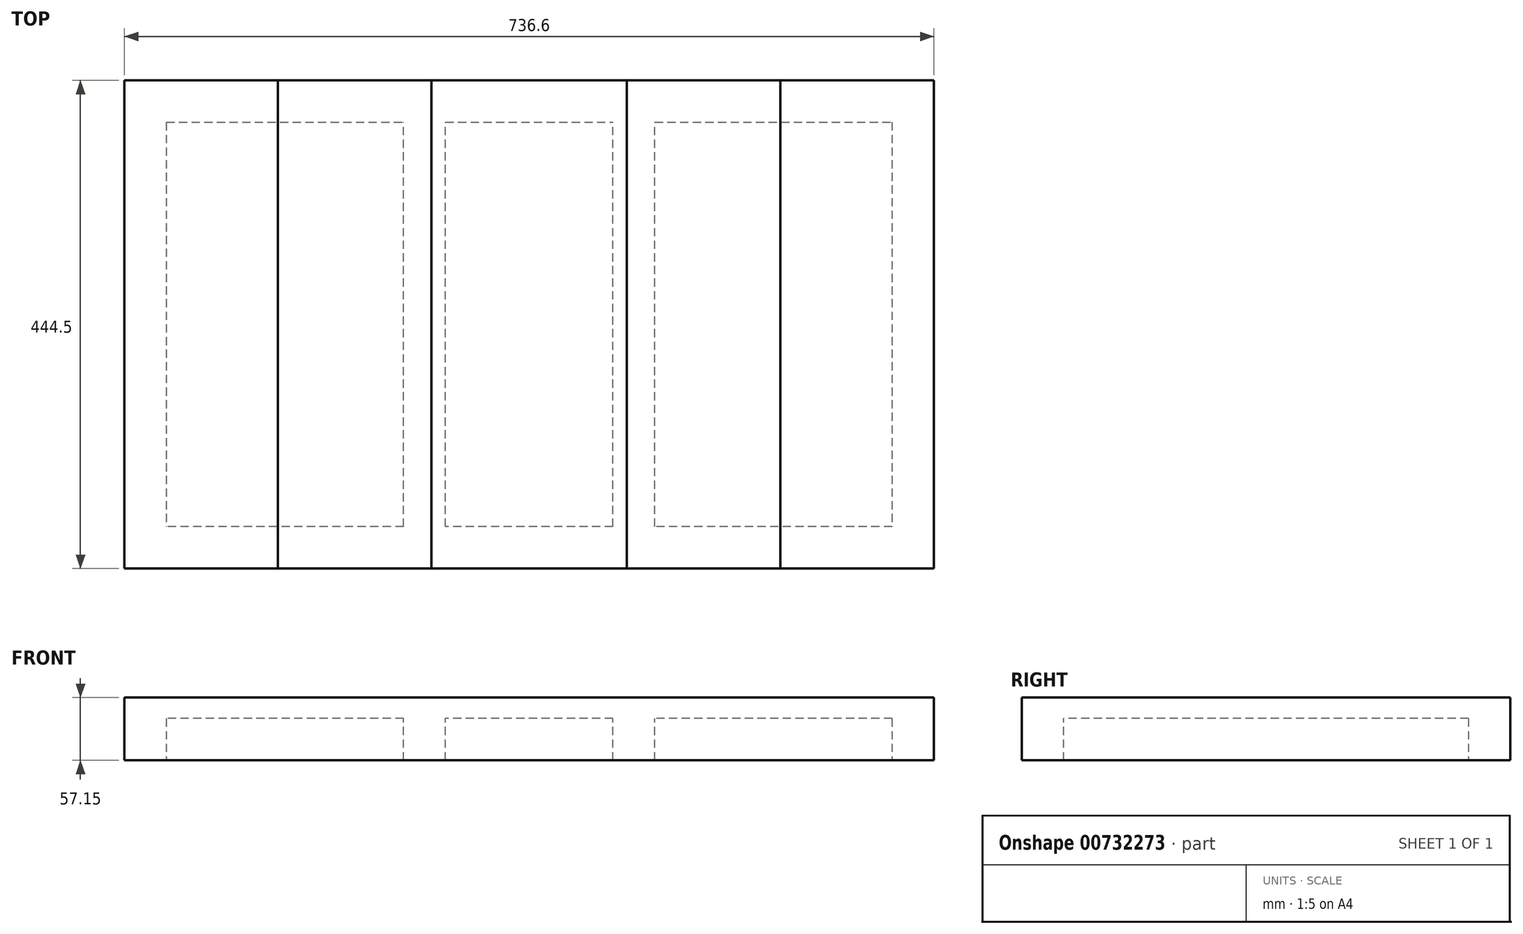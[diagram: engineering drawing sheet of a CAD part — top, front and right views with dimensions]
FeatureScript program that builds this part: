
annotation { "Feature Type Name" : "Feature", "Feature Type Description" : "" }
export const myFeature = defineFeature(function(context is Context, id is Id, definition is map)
    precondition{}
    {
        {
            var Q0;
            Q0=qCreatedBy(makeId("Right.planeOp"),FACE);
            var sketch = newSketch(context, id + "F0", { "sketchPlane" : qUnion([Q0])});
            skLineSegment(sketch, "E0.bottom", {"start": v(0, 0) * mm, "end": v(-38.1, 0) * mm});
            skLineSegment(sketch, "E0.top", {"start": v(0, -38.1) * mm, "end": v(-38.1, -38.1) * mm});
            skLineSegment(sketch, "E0.left", {"start": v(0, 0) * mm, "end": v(0, -38.1) * mm});
            skLineSegment(sketch, "E0.right", {"start": v(-38.1, 0) * mm, "end": v(-38.1, -38.1) * mm});
            skSolve(sketch);
        }
        {
            var Q0;
            Q0=makeQuery(id+"F0.imprint","IMPRINT",FACE,{"disambiguationData":[TD([[makeQuery(id+"F0.imprint","IMPRINT",EDGE,{"derivedFrom":sQuery(id+"F0.wireOp",EDGE,"E0.bottom")}),1.0]])]});
            extrude(context, id + "F1", {"entities" : qUnion([Q0]), "depth" : 736.6 * mm, "offsetDistance" : 25.4 * mm});
        }
        {
            var Q0;
            Q0=makeQuery(id+"F1.opExtrude","SWEPT_FACE",FACE,{"disambiguationData":[OSD([sQuery(id+"F0.wireOp",EDGE,"E0.left")])]});
            var sketch = newSketch(context, id + "F2", { "sketchPlane" : qUnion([Q0])});
            skLineSegment(sketch, "E1.bottom", {"start": v(-736.6, 0) * mm, "end": v(-698.5, 0) * mm});
            skLineSegment(sketch, "E1.top", {"start": v(-736.6, -38.1) * mm, "end": v(-698.5, -38.1) * mm});
            skLineSegment(sketch, "E1.left", {"start": v(-736.6, 0) * mm, "end": v(-736.6, -38.1) * mm});
            skLineSegment(sketch, "E1.right", {"start": v(-698.5, 0) * mm, "end": v(-698.5, -38.1) * mm});
            skLineSegment(sketch, "E2.bottom", {"start": v(0, 0) * mm, "end": v(-38.1, 0) * mm});
            skLineSegment(sketch, "E2.top", {"start": v(0, -38.1) * mm, "end": v(-38.1, -38.1) * mm});
            skLineSegment(sketch, "E2.left", {"start": v(0, 0) * mm, "end": v(0, -38.1) * mm});
            skLineSegment(sketch, "E2.right", {"start": v(-38.1, 0) * mm, "end": v(-38.1, -38.1) * mm});
            skSolve(sketch);
        }
        {
            var Q0;
            Q0=makeQuery(id+"F2.imprint","IMPRINT",FACE,{"disambiguationData":[TD([[makeQuery(id+"F2.imprint","IMPRINT",EDGE,{"derivedFrom":sQuery(id+"F2.wireOp",EDGE,"E2.bottom")}),-1.0]])]});
            var Q1;
            Q1=makeQuery(id+"F2.imprint","IMPRINT",FACE,{"disambiguationData":[TD([[makeQuery(id+"F2.imprint","IMPRINT",EDGE,{"derivedFrom":sQuery(id+"F2.wireOp",EDGE,"E1.bottom")}),-1.0]])]});
            extrude(context, id + "F3", {"entities" : qUnion([Q0, Q1]), "operationType" : NewBodyOperationType.ADD, "depth" : 368.3 * mm, "offsetDistance" : 25.4 * mm});
        }
        {
            var Q0;
            Q0=makeQuery(id+"F3.boolean.opBoolean","MERGE",FACE,{"derivedFrom":[makeQuery(id+"F1.opExtrude","CAP_FACE",FACE,{"disambiguationData":[OSD([sQuery(id+"F0.wireOp",EDGE,"E0.bottom"),sQuery(id+"F0.wireOp",EDGE,"E0.top"),sQuery(id+"F0.wireOp",EDGE,"E0.left"),sQuery(id+"F0.wireOp",EDGE,"E0.right")])],"isStart":false}),makeQuery(id+"F3.opExtrude","SWEPT_FACE",FACE,{"disambiguationData":[OSD([sQuery(id+"F2.wireOp",EDGE,"E1.left")])]})]});
            var sketch = newSketch(context, id + "F4", { "sketchPlane" : qUnion([Q0])});
            skLineSegment(sketch, "E3.bottom", {"start": v(368.3, 0) * mm, "end": v(406.4, 0) * mm});
            skLineSegment(sketch, "E3.top", {"start": v(368.3, -38.1) * mm, "end": v(406.4, -38.1) * mm});
            skLineSegment(sketch, "E3.left", {"start": v(368.3, 0) * mm, "end": v(368.3, -38.1) * mm});
            skLineSegment(sketch, "E3.right", {"start": v(406.4, 0) * mm, "end": v(406.4, -38.1) * mm});
            skSolve(sketch);
        }
        {
            var Q0;
            Q0=makeQuery(id+"F4.imprint","IMPRINT",FACE,{"disambiguationData":[TD([[makeQuery(id+"F4.imprint","IMPRINT",EDGE,{"derivedFrom":sQuery(id+"F4.wireOp",EDGE,"E3.bottom")}),-1.0]])]});
            extrude(context, id + "F5", {"entities" : qUnion([Q0]), "operationType" : NewBodyOperationType.ADD, "oppositeDirection" : true, "depth" : 736.6 * mm, "offsetDistance" : 25.4 * mm});
        }
        {
            var Q0;
            Q0=makeQuery(id+"F5.opExtrude","SWEPT_FACE",FACE,{"disambiguationData":[OSD([sQuery(id+"F4.wireOp",EDGE,"E3.left")])]});
            var sketch = newSketch(context, id + "F6", { "sketchPlane" : qUnion([Q0])});
            skLineSegment(sketch, "E4.bottom", {"start": v(254, 0) * mm, "end": v(292.1, 0) * mm});
            skLineSegment(sketch, "E4.top", {"start": v(254, -38.1) * mm, "end": v(292.1, -38.1) * mm});
            skLineSegment(sketch, "E4.left", {"start": v(254, 0) * mm, "end": v(254, -38.1) * mm});
            skLineSegment(sketch, "E4.right", {"start": v(292.1, 0) * mm, "end": v(292.1, -38.1) * mm});
            skLineSegment(sketch, "E5.bottom", {"start": v(444.5, 0) * mm, "end": v(482.6, 0) * mm});
            skLineSegment(sketch, "E5.top", {"start": v(444.5, -38.1) * mm, "end": v(482.6, -38.1) * mm});
            skLineSegment(sketch, "E5.left", {"start": v(444.5, 0) * mm, "end": v(444.5, -38.1) * mm});
            skLineSegment(sketch, "E5.right", {"start": v(482.6, 0) * mm, "end": v(482.6, -38.1) * mm});
            skSolve(sketch);
        }
        {
            var Q0;
            Q0=makeQuery(id+"F6.imprint","IMPRINT",FACE,{"disambiguationData":[TD([[makeQuery(id+"F6.imprint","IMPRINT",EDGE,{"derivedFrom":sQuery(id+"F6.wireOp",EDGE,"E4.bottom")}),-1.0]])]});
            var Q1;
            Q1=makeQuery(id+"F6.imprint","IMPRINT",FACE,{"disambiguationData":[TD([[makeQuery(id+"F6.imprint","IMPRINT",EDGE,{"derivedFrom":sQuery(id+"F6.wireOp",EDGE,"E5.bottom")}),-1.0]])]});
            extrude(context, id + "F7", {"entities" : qUnion([Q0, Q1]), "operationType" : NewBodyOperationType.ADD, "endBound" : BoundingType.UP_TO_NEXT, "depth" : 25.4 * mm, "offsetDistance" : 25.4 * mm});
        }
        {
            var Q0;
            Q0=makeQuery(id+"F7.boolean.opBoolean","MERGE",FACE,{"derivedFrom":[makeQuery(id+"F5.boolean.opBoolean","MERGE",FACE,{"derivedFrom":[makeQuery(id+"F3.boolean.opBoolean","MERGE",FACE,{"derivedFrom":[makeQuery(id+"F1.opExtrude","SWEPT_FACE",FACE,{"disambiguationData":[OSD([sQuery(id+"F0.wireOp",EDGE,"E0.bottom")])]}),makeQuery(id+"F3.opExtrude","SWEPT_FACE",FACE,{"disambiguationData":[OSD([sQuery(id+"F2.wireOp",EDGE,"E1.bottom")])]}),makeQuery(id+"F3.opExtrude","SWEPT_FACE",FACE,{"disambiguationData":[OSD([sQuery(id+"F2.wireOp",EDGE,"E2.bottom")])]})]}),makeQuery(id+"F5.opExtrude","SWEPT_FACE",FACE,{"disambiguationData":[OSD([sQuery(id+"F4.wireOp",EDGE,"E3.bottom")])]})]}),makeQuery(id+"F7.opExtrude","SWEPT_FACE",FACE,{"disambiguationData":[OSD([sQuery(id+"F6.wireOp",EDGE,"E4.bottom")])]}),makeQuery(id+"F7.opExtrude","SWEPT_FACE",FACE,{"disambiguationData":[OSD([sQuery(id+"F6.wireOp",EDGE,"E5.bottom")])]})]});
            var sketch = newSketch(context, id + "F8", { "sketchPlane" : qUnion([Q0])});
            skLineSegment(sketch, "E6.bottom", {"start": v(0, 406.4) * mm, "end": v(139.7, 406.4) * mm});
            skLineSegment(sketch, "E6.top", {"start": v(0, -38.1) * mm, "end": v(139.7, -38.1) * mm});
            skLineSegment(sketch, "E6.left", {"start": v(0, 406.4) * mm, "end": v(0, -38.1) * mm});
            skLineSegment(sketch, "E6.right", {"start": v(139.7, 406.4) * mm, "end": v(139.7, -38.1) * mm});
            skSolve(sketch);
        }
        {
            var Q0;
            {var subQ1=sQuery(id+"F8.wireOp",EDGE,"E6.bottom");Q0=makeQuery(id+"F8.imprint","IMPRINT",FACE,{"disambiguationData":[TD([[makeQuery(id+"F8.imprint","IMPRINT",EDGE,{"derivedFrom":subQ1}),-1.0]])]});}
            var Q1;
            {var subQ1=sQuery(id+"F2.wireOp",EDGE,"E2.right");var subQ5=sQuery(id+"F2.wireOp",EDGE,"E2.bottom");var subQ7=sQuery(id+"F0.wireOp",EDGE,"E0.bottom");var subQ17=sQuery(id+"F0.wireOp",EDGE,"E0.left");var subQ20=makeQuery(id+"F3.opExtrude","SWEPT_EDGE",EDGE,{"disambiguationData":[OSD([subQ7,subQ17,subQ5,subQ1])]});Q1=makeQuery(id+"F8.imprint","IMPRINT",FACE,{"disambiguationData":[TD([[makeQuery(id+"F8.imprint","IMPRINT",EDGE,{"derivedFrom":subQ20}),1.0]])]});}
            extrude(context, id + "F9", {"entities" : qUnion([Q0, Q1]), "operationType" : NewBodyOperationType.ADD, "depth" : 19.05 * mm, "offsetDistance" : 25.4 * mm});
        }
        {
            var Q0;
            Q0=makeQuery(id+"F7.boolean.opBoolean","MERGE",FACE,{"derivedFrom":[makeQuery(id+"F5.boolean.opBoolean","MERGE",FACE,{"derivedFrom":[makeQuery(id+"F3.boolean.opBoolean","MERGE",FACE,{"derivedFrom":[makeQuery(id+"F1.opExtrude","SWEPT_FACE",FACE,{"disambiguationData":[OSD([sQuery(id+"F0.wireOp",EDGE,"E0.bottom")])]}),makeQuery(id+"F3.opExtrude","SWEPT_FACE",FACE,{"disambiguationData":[OSD([sQuery(id+"F2.wireOp",EDGE,"E1.bottom")])]}),makeQuery(id+"F3.opExtrude","SWEPT_FACE",FACE,{"disambiguationData":[OSD([sQuery(id+"F2.wireOp",EDGE,"E2.bottom")])]})]}),makeQuery(id+"F5.opExtrude","SWEPT_FACE",FACE,{"disambiguationData":[OSD([sQuery(id+"F4.wireOp",EDGE,"E3.bottom")])]})]}),makeQuery(id+"F7.opExtrude","SWEPT_FACE",FACE,{"disambiguationData":[OSD([sQuery(id+"F6.wireOp",EDGE,"E4.bottom")])]}),makeQuery(id+"F7.opExtrude","SWEPT_FACE",FACE,{"disambiguationData":[OSD([sQuery(id+"F6.wireOp",EDGE,"E5.bottom")])]})]});
            var sketch = newSketch(context, id + "F10", { "sketchPlane" : qUnion([Q0])});
            skLineSegment(sketch, "E7.bottom", {"start": v(736.6, 406.4) * mm, "end": v(596.9, 406.4) * mm});
            skLineSegment(sketch, "E7.top", {"start": v(736.6, -38.1) * mm, "end": v(596.9, -38.1) * mm});
            skLineSegment(sketch, "E7.left", {"start": v(736.6, 406.4) * mm, "end": v(736.6, -38.1) * mm});
            skLineSegment(sketch, "E7.right", {"start": v(596.9, 406.4) * mm, "end": v(596.9, -38.1) * mm});
            skSolve(sketch);
        }
        {
            var Q0;
            {var subQ2=sQuery(id+"F2.wireOp",EDGE,"E1.right");var subQ6=sQuery(id+"F2.wireOp",EDGE,"E1.bottom");var subQ8=sQuery(id+"F0.wireOp",EDGE,"E0.bottom");var subQ16=sQuery(id+"F0.wireOp",EDGE,"E0.left");var subQ19=makeQuery(id+"F3.opExtrude","SWEPT_EDGE",EDGE,{"disambiguationData":[OSD([subQ8,subQ16,subQ6,subQ2])]});Q0=makeQuery(id+"F10.imprint","IMPRINT",FACE,{"disambiguationData":[TD([[makeQuery(id+"F10.imprint","IMPRINT",EDGE,{"derivedFrom":subQ19}),-1.0]])]});}
            var Q1;
            {var subQ1=sQuery(id+"F10.wireOp",EDGE,"E7.bottom");Q1=makeQuery(id+"F10.imprint","IMPRINT",FACE,{"disambiguationData":[TD([[makeQuery(id+"F10.imprint","IMPRINT",EDGE,{"derivedFrom":subQ1}),-1.0]])]});}
            extrude(context, id + "F11", {"entities" : qUnion([Q0, Q1]), "operationType" : NewBodyOperationType.ADD, "depth" : 19.05 * mm, "offsetDistance" : 25.4 * mm});
        }
        {
            var Q0;
            Q0=makeQuery(id+"F7.boolean.opBoolean","MERGE",FACE,{"derivedFrom":[makeQuery(id+"F5.boolean.opBoolean","MERGE",FACE,{"derivedFrom":[makeQuery(id+"F3.boolean.opBoolean","MERGE",FACE,{"derivedFrom":[makeQuery(id+"F1.opExtrude","SWEPT_FACE",FACE,{"disambiguationData":[OSD([sQuery(id+"F0.wireOp",EDGE,"E0.bottom")])]}),makeQuery(id+"F3.opExtrude","SWEPT_FACE",FACE,{"disambiguationData":[OSD([sQuery(id+"F2.wireOp",EDGE,"E1.bottom")])]}),makeQuery(id+"F3.opExtrude","SWEPT_FACE",FACE,{"disambiguationData":[OSD([sQuery(id+"F2.wireOp",EDGE,"E2.bottom")])]})]}),makeQuery(id+"F5.opExtrude","SWEPT_FACE",FACE,{"disambiguationData":[OSD([sQuery(id+"F4.wireOp",EDGE,"E3.bottom")])]})]}),makeQuery(id+"F7.opExtrude","SWEPT_FACE",FACE,{"disambiguationData":[OSD([sQuery(id+"F6.wireOp",EDGE,"E4.bottom")])]}),makeQuery(id+"F7.opExtrude","SWEPT_FACE",FACE,{"disambiguationData":[OSD([sQuery(id+"F6.wireOp",EDGE,"E5.bottom")])]})]});
            var sketch = newSketch(context, id + "F12", { "sketchPlane" : qUnion([Q0])});
            skLineSegment(sketch, "E8.bottom", {"start": v(139.7, 406.4) * mm, "end": v(279.4, 406.4) * mm});
            skLineSegment(sketch, "E8.top", {"start": v(139.7, -38.1) * mm, "end": v(279.4, -38.1) * mm});
            skLineSegment(sketch, "E8.left", {"start": v(139.7, 406.4) * mm, "end": v(139.7, -38.1) * mm});
            skLineSegment(sketch, "E8.right", {"start": v(279.4, 406.4) * mm, "end": v(279.4, -38.1) * mm});
            skSolve(sketch);
        }
        {
            var Q0;
            {var subQ18=sQuery(id+"F12.wireOp",EDGE,"E8.bottom");Q0=makeQuery(id+"F12.imprint","IMPRINT",FACE,{"disambiguationData":[TD([[makeQuery(id+"F12.imprint","IMPRINT",EDGE,{"derivedFrom":subQ18}),-1.0]])]});}
            var Q1;
            {var subQ1=sQuery(id+"F2.wireOp",EDGE,"E1.bottom");var subQ6=sQuery(id+"F0.wireOp",EDGE,"E0.bottom");var subQ8=sQuery(id+"F6.wireOp",EDGE,"E4.bottom");var subQ10=sQuery(id+"F4.wireOp",EDGE,"E3.bottom");var subQ14=sQuery(id+"F6.wireOp",EDGE,"E4.left");var subQ17=sQuery(id+"F4.wireOp",EDGE,"E3.left");var subQ19=sQuery(id+"F2.wireOp",EDGE,"E1.left");Q1=makeQuery(id+"F12.imprint","IMPRINT",FACE,{"disambiguationData":[TD([[makeQuery(id+"F12.imprint","IMPRINT",EDGE,{"derivedFrom":makeQuery(id+"F7.opExtrude","SWEPT_EDGE",EDGE,{"disambiguationData":[OSD([subQ6,subQ1,subQ19,subQ10,subQ17,subQ8,subQ14])]})}),1.0]])]});}
            extrude(context, id + "F13", {"entities" : qUnion([Q0, Q1]), "operationType" : NewBodyOperationType.ADD, "depth" : 19.02 * mm, "offsetDistance" : 25.4 * mm});
        }
        {
            var Q0;
            Q0=makeQuery(id+"F7.boolean.opBoolean","MERGE",FACE,{"derivedFrom":[makeQuery(id+"F5.boolean.opBoolean","MERGE",FACE,{"derivedFrom":[makeQuery(id+"F3.boolean.opBoolean","MERGE",FACE,{"derivedFrom":[makeQuery(id+"F1.opExtrude","SWEPT_FACE",FACE,{"disambiguationData":[OSD([sQuery(id+"F0.wireOp",EDGE,"E0.bottom")])]}),makeQuery(id+"F3.opExtrude","SWEPT_FACE",FACE,{"disambiguationData":[OSD([sQuery(id+"F2.wireOp",EDGE,"E1.bottom")])]}),makeQuery(id+"F3.opExtrude","SWEPT_FACE",FACE,{"disambiguationData":[OSD([sQuery(id+"F2.wireOp",EDGE,"E2.bottom")])]})]}),makeQuery(id+"F5.opExtrude","SWEPT_FACE",FACE,{"disambiguationData":[OSD([sQuery(id+"F4.wireOp",EDGE,"E3.bottom")])]})]}),makeQuery(id+"F7.opExtrude","SWEPT_FACE",FACE,{"disambiguationData":[OSD([sQuery(id+"F6.wireOp",EDGE,"E4.bottom")])]}),makeQuery(id+"F7.opExtrude","SWEPT_FACE",FACE,{"disambiguationData":[OSD([sQuery(id+"F6.wireOp",EDGE,"E5.bottom")])]})]});
            var sketch = newSketch(context, id + "F14", { "sketchPlane" : qUnion([Q0])});
            skLineSegment(sketch, "E9.bottom", {"start": v(596.9, 406.4) * mm, "end": v(457.2, 406.4) * mm});
            skLineSegment(sketch, "E9.top", {"start": v(596.9, -38.1) * mm, "end": v(457.2, -38.1) * mm});
            skLineSegment(sketch, "E9.left", {"start": v(596.9, 406.4) * mm, "end": v(596.9, -38.1) * mm});
            skLineSegment(sketch, "E9.right", {"start": v(457.2, 406.4) * mm, "end": v(457.2, -38.1) * mm});
            skSolve(sketch);
        }
        {
            var Q0;
            {var subQ18=sQuery(id+"F14.wireOp",EDGE,"E9.bottom");Q0=makeQuery(id+"F14.imprint","IMPRINT",FACE,{"disambiguationData":[TD([[makeQuery(id+"F14.imprint","IMPRINT",EDGE,{"derivedFrom":subQ18}),-1.0]])]});}
            var Q1;
            {var subQ1=sQuery(id+"F2.wireOp",EDGE,"E1.bottom");var subQ6=sQuery(id+"F0.wireOp",EDGE,"E0.bottom");var subQ9=sQuery(id+"F4.wireOp",EDGE,"E3.bottom");var subQ11=sQuery(id+"F6.wireOp",EDGE,"E5.bottom");var subQ14=sQuery(id+"F6.wireOp",EDGE,"E5.right");var subQ17=sQuery(id+"F4.wireOp",EDGE,"E3.left");var subQ19=sQuery(id+"F2.wireOp",EDGE,"E1.left");Q1=makeQuery(id+"F14.imprint","IMPRINT",FACE,{"disambiguationData":[TD([[makeQuery(id+"F14.imprint","IMPRINT",EDGE,{"derivedFrom":makeQuery(id+"F7.opExtrude","SWEPT_EDGE",EDGE,{"disambiguationData":[OSD([subQ6,subQ1,subQ19,subQ9,subQ17,subQ11,subQ14])]})}),-1.0]])]});}
            extrude(context, id + "F15", {"entities" : qUnion([Q0, Q1]), "operationType" : NewBodyOperationType.ADD, "depth" : 19.02 * mm, "offsetDistance" : 25.4 * mm});
        }
        {
            var Q0;
            Q0=makeQuery(id+"F7.boolean.opBoolean","MERGE",FACE,{"derivedFrom":[makeQuery(id+"F5.boolean.opBoolean","MERGE",FACE,{"derivedFrom":[makeQuery(id+"F3.boolean.opBoolean","MERGE",FACE,{"derivedFrom":[makeQuery(id+"F1.opExtrude","SWEPT_FACE",FACE,{"disambiguationData":[OSD([sQuery(id+"F0.wireOp",EDGE,"E0.bottom")])]}),makeQuery(id+"F3.opExtrude","SWEPT_FACE",FACE,{"disambiguationData":[OSD([sQuery(id+"F2.wireOp",EDGE,"E1.bottom")])]}),makeQuery(id+"F3.opExtrude","SWEPT_FACE",FACE,{"disambiguationData":[OSD([sQuery(id+"F2.wireOp",EDGE,"E2.bottom")])]})]}),makeQuery(id+"F5.opExtrude","SWEPT_FACE",FACE,{"disambiguationData":[OSD([sQuery(id+"F4.wireOp",EDGE,"E3.bottom")])]})]}),makeQuery(id+"F7.opExtrude","SWEPT_FACE",FACE,{"disambiguationData":[OSD([sQuery(id+"F6.wireOp",EDGE,"E4.bottom")])]}),makeQuery(id+"F7.opExtrude","SWEPT_FACE",FACE,{"disambiguationData":[OSD([sQuery(id+"F6.wireOp",EDGE,"E5.bottom")])]})]});
            var sketch = newSketch(context, id + "F16", { "sketchPlane" : qUnion([Q0])});
            skLineSegment(sketch, "E10.bottom", {"start": v(279.4, 406.4) * mm, "end": v(457.2, 406.4) * mm});
            skLineSegment(sketch, "E10.top", {"start": v(279.4, -38.1) * mm, "end": v(457.2, -38.1) * mm});
            skLineSegment(sketch, "E10.left", {"start": v(279.4, 406.4) * mm, "end": v(279.4, -38.1) * mm});
            skLineSegment(sketch, "E10.right", {"start": v(457.2, 406.4) * mm, "end": v(457.2, -38.1) * mm});
            skSolve(sketch);
        }
        {
            var Q0;
            Q0=makeQuery(id+"F16.imprint","IMPRINT",FACE,{"disambiguationData":[TD([[makeQuery(id+"F16.imprint","IMPRINT",EDGE,{"derivedFrom":sQuery(id+"F16.wireOp",EDGE,"E10.bottom")}),-1.0]])]});
            var Q1;
            {var subQ0=sQuery(id+"F6.wireOp",EDGE,"E4.right");var subQ1=sQuery(id+"F6.wireOp",EDGE,"E4.bottom");var subQ2=sQuery(id+"F4.wireOp",EDGE,"E3.left");var subQ3=sQuery(id+"F4.wireOp",EDGE,"E3.bottom");var subQ4=sQuery(id+"F2.wireOp",EDGE,"E1.left");var subQ5=sQuery(id+"F2.wireOp",EDGE,"E1.bottom");var subQ6=sQuery(id+"F0.wireOp",EDGE,"E0.bottom");Q1=makeQuery(id+"F16.imprint","IMPRINT",FACE,{"disambiguationData":[TD([[makeQuery(id+"F16.imprint","IMPRINT",EDGE,{"derivedFrom":makeQuery(id+"F7.opExtrude","SWEPT_EDGE",EDGE,{"disambiguationData":[OSD([subQ6,subQ5,subQ4,subQ3,subQ2,subQ1,subQ0])]})}),-1.0]])]});}
            extrude(context, id + "F17", {"entities" : qUnion([Q0, Q1]), "operationType" : NewBodyOperationType.ADD, "depth" : 19.05 * mm, "offsetDistance" : 25.4 * mm});
        }
    });
